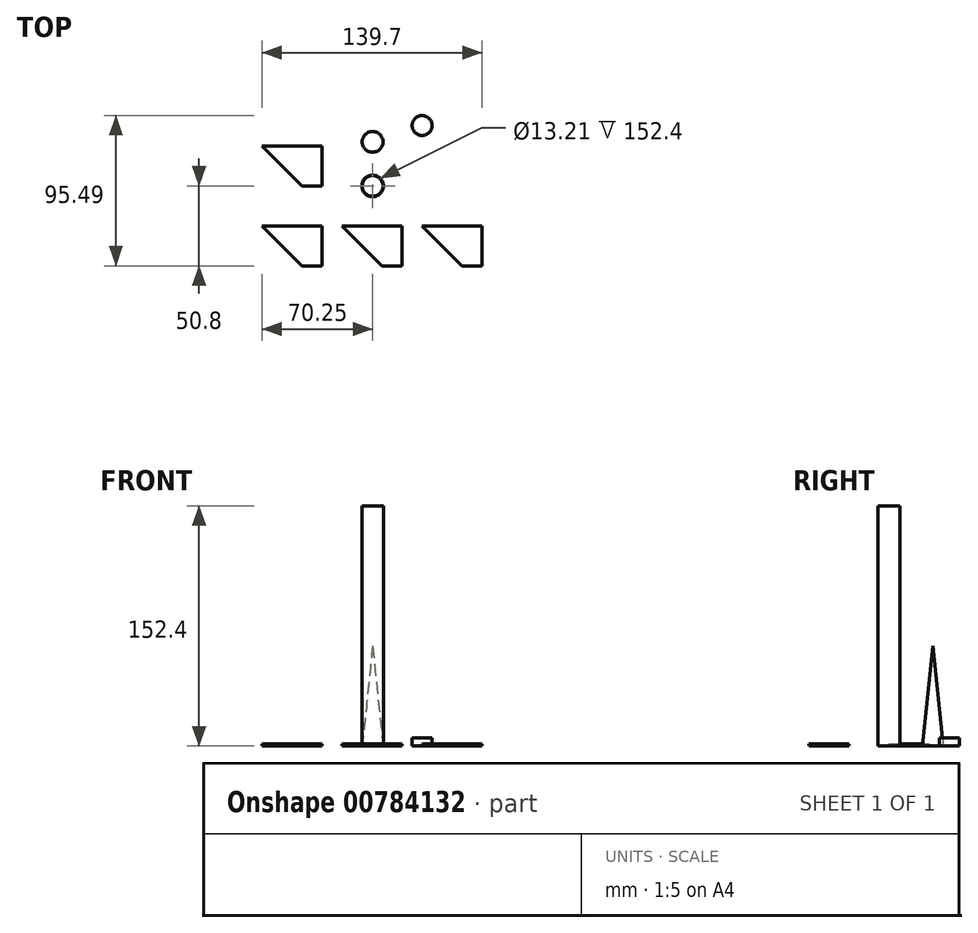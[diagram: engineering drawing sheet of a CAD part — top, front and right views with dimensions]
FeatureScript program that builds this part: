
annotation { "Feature Type Name" : "Feature", "Feature Type Description" : "" }
export const myFeature = defineFeature(function(context is Context, id is Id, definition is map)
    precondition{}
    {
        {
            var Q0;
            Q0=qCreatedBy(makeId("Top.planeOp"),FACE);
            var sketch = newSketch(context, id + "F0", { "sketchPlane" : qUnion([Q0])});
            skCircle(sketch, "E0", {"center": v(0, 0) * mm, "radius": 6.86 * mm});
            skSolve(sketch);
        }
        {
            var Q0;
            Q0=makeQuery(id+"F0.imprint","IMPRINT",FACE,{"disambiguationData":[TD([[makeQuery(id+"F0.imprint","IMPRINT",EDGE,{"derivedFrom":sQuery(id+"F0.wireOp",EDGE,"E0")}),1.0]])]});
            extrude(context, id + "F1", {"entities" : qUnion([Q0]), "depth" : 152.4 * mm, "offsetDistance" : 25.4 * mm});
        }
        {
            var Q0;
            Q0=makeQuery(id+"F1.opExtrude","CAP_FACE",FACE,{"disambiguationData":[OSD([sQuery(id+"F0.wireOp",EDGE,"E0")])],"isStart":false});
            var sketch = newSketch(context, id + "F2", { "sketchPlane" : qUnion([Q0])});
            skCircle(sketch, "E1", {"center": v(0, 0) * mm, "radius": 6.6 * mm});
            skSolve(sketch);
        }
        {
            var Q0;
            Q0=makeQuery(id+"F2.imprint","IMPRINT",FACE,{"disambiguationData":[TD([[makeQuery(id+"F2.imprint","IMPRINT",EDGE,{"derivedFrom":sQuery(id+"F2.wireOp",EDGE,"E1")}),1.0]])]});
            extrude(context, id + "F3", {"entities" : qUnion([Q0]), "operationType" : NewBodyOperationType.REMOVE, "oppositeDirection" : true, "depth" : 304.8 * mm, "offsetDistance" : 25.4 * mm});
        }
        {
            var Q0;
            Q0=qCreatedBy(makeId("Right.planeOp"),FACE);
            var sketch = newSketch(context, id + "F4", { "sketchPlane" : qUnion([Q0])});
            skLineSegment(sketch, "E2", {"start": v(27.98, 0) * mm, "end": v(27.98, 63.5) * mm});
            skLineSegment(sketch, "E3", {"start": v(27.98, 63.5) * mm, "end": v(34.58, 0) * mm});
            skLineSegment(sketch, "E4", {"start": v(34.58, 0) * mm, "end": v(27.98, 0) * mm});
            skSolve(sketch);
        }
        {
            var Q0;
            Q0=makeQuery(id+"F4.imprint","IMPRINT",FACE,{"disambiguationData":[TD([[makeQuery(id+"F4.imprint","IMPRINT",EDGE,{"derivedFrom":sQuery(id+"F4.wireOp",EDGE,"E2")}),-1.0]])]});
            var Q1;
            Q1=sQuery(id+"F4.wireOp",EDGE,"E2");
            revolve(context, id + "F5", {"surfaceOperationType" : NewSurfaceOperationType.NEW, "entities" : qUnion([Q0]), "axis" : qUnion([Q1]), "revolveType" : RevolveType.FULL});
        }
        {
            var Q0;
            Q0=qCreatedBy(makeId("Top.planeOp"),FACE);
            var sketch = newSketch(context, id + "F6", { "sketchPlane" : qUnion([Q0])});
            skLineSegment(sketch, "E5", {"start": v(-32.15, 0) * mm, "end": v(-32.15, 25.4) * mm});
            skLineSegment(sketch, "E6", {"start": v(-32.15, 0) * mm, "end": v(-44.85, 0) * mm});
            skLineSegment(sketch, "E7", {"start": v(-32.15, 25.4) * mm, "end": v(-70.25, 25.4) * mm});
            skLineSegment(sketch, "E8", {"start": v(-44.85, 0) * mm, "end": v(-70.25, 25.4) * mm});
            skSolve(sketch);
        }
        {
            var Q0;
            Q0=makeQuery(id+"F6.imprint","IMPRINT",FACE,{"disambiguationData":[TD([[makeQuery(id+"F6.imprint","IMPRINT",EDGE,{"derivedFrom":sQuery(id+"F6.wireOp",EDGE,"E5")}),1.0]])]});
            extrude(context, id + "F7", {"entities" : qUnion([Q0]), "depth" : 1.27 * mm, "offsetDistance" : 25.4 * mm});
        }
        {
            var Q0;
            Q0=makeQuery(id+"F7.opExtrude","SWEPT_BODY",BODY,{"disambiguationData":[OSD([sQuery(id+"F6.wireOp",EDGE,"E5"),sQuery(id+"F6.wireOp",EDGE,"E6"),sQuery(id+"F6.wireOp",EDGE,"E7"),sQuery(id+"F6.wireOp",EDGE,"E8")])]});
            transform(context, id + "F8", {"entities" : qUnion([Q0]), "transformType" : TransformType.TRANSLATION_3D, "dx" : 0 * mm, "dy" : -50.8 * mm, "dz" : 0 * mm, "makeCopy" : true});
        }
        {
            var Q0;
            Q0=makeQuery(id+"F8.opPattern","COPY",BODY,{"derivedFrom":makeQuery(id+"F7.opExtrude","SWEPT_BODY",BODY,{"disambiguationData":[OSD([sQuery(id+"F6.wireOp",EDGE,"E5"),sQuery(id+"F6.wireOp",EDGE,"E6"),sQuery(id+"F6.wireOp",EDGE,"E7"),sQuery(id+"F6.wireOp",EDGE,"E8")])]}),"instanceName":"1"});
            transform(context, id + "F9", {"entities" : qUnion([Q0]), "transformType" : TransformType.TRANSLATION_3D, "dx" : 50.8 * mm, "dy" : 0 * mm, "dz" : 0 * mm, "makeCopy" : true});
        }
        {
            var Q0;
            Q0=makeQuery(id+"F9.opPattern","COPY",BODY,{"derivedFrom":makeQuery(id+"F8.opPattern","COPY",BODY,{"derivedFrom":makeQuery(id+"F7.opExtrude","SWEPT_BODY",BODY,{"disambiguationData":[OSD([sQuery(id+"F6.wireOp",EDGE,"E5"),sQuery(id+"F6.wireOp",EDGE,"E6"),sQuery(id+"F6.wireOp",EDGE,"E7"),sQuery(id+"F6.wireOp",EDGE,"E8")])]}),"instanceName":"1"}),"instanceName":"1"});
            transform(context, id + "F10", {"entities" : qUnion([Q0]), "transformType" : TransformType.TRANSLATION_3D, "dx" : 50.8 * mm, "dy" : 0 * mm, "dz" : 0 * mm, "makeCopy" : true});
        }
        {
            var Q0;
            Q0=qCreatedBy(makeId("Top.planeOp"),FACE);
            var sketch = newSketch(context, id + "F11", { "sketchPlane" : qUnion([Q0])});
            skCircle(sketch, "E9", {"center": v(31.43, 38.35) * mm, "radius": 6.34 * mm});
            skSolve(sketch);
        }
        {
            var Q0;
            Q0=makeQuery(id+"F11.imprint","IMPRINT",FACE,{"disambiguationData":[TD([[makeQuery(id+"F11.imprint","IMPRINT",EDGE,{"derivedFrom":sQuery(id+"F11.wireOp",EDGE,"E9")}),1.0]])]});
            extrude(context, id + "F12", {"entities" : qUnion([Q0]), "depth" : 5.08 * mm, "offsetDistance" : 25.4 * mm});
        }
    });
